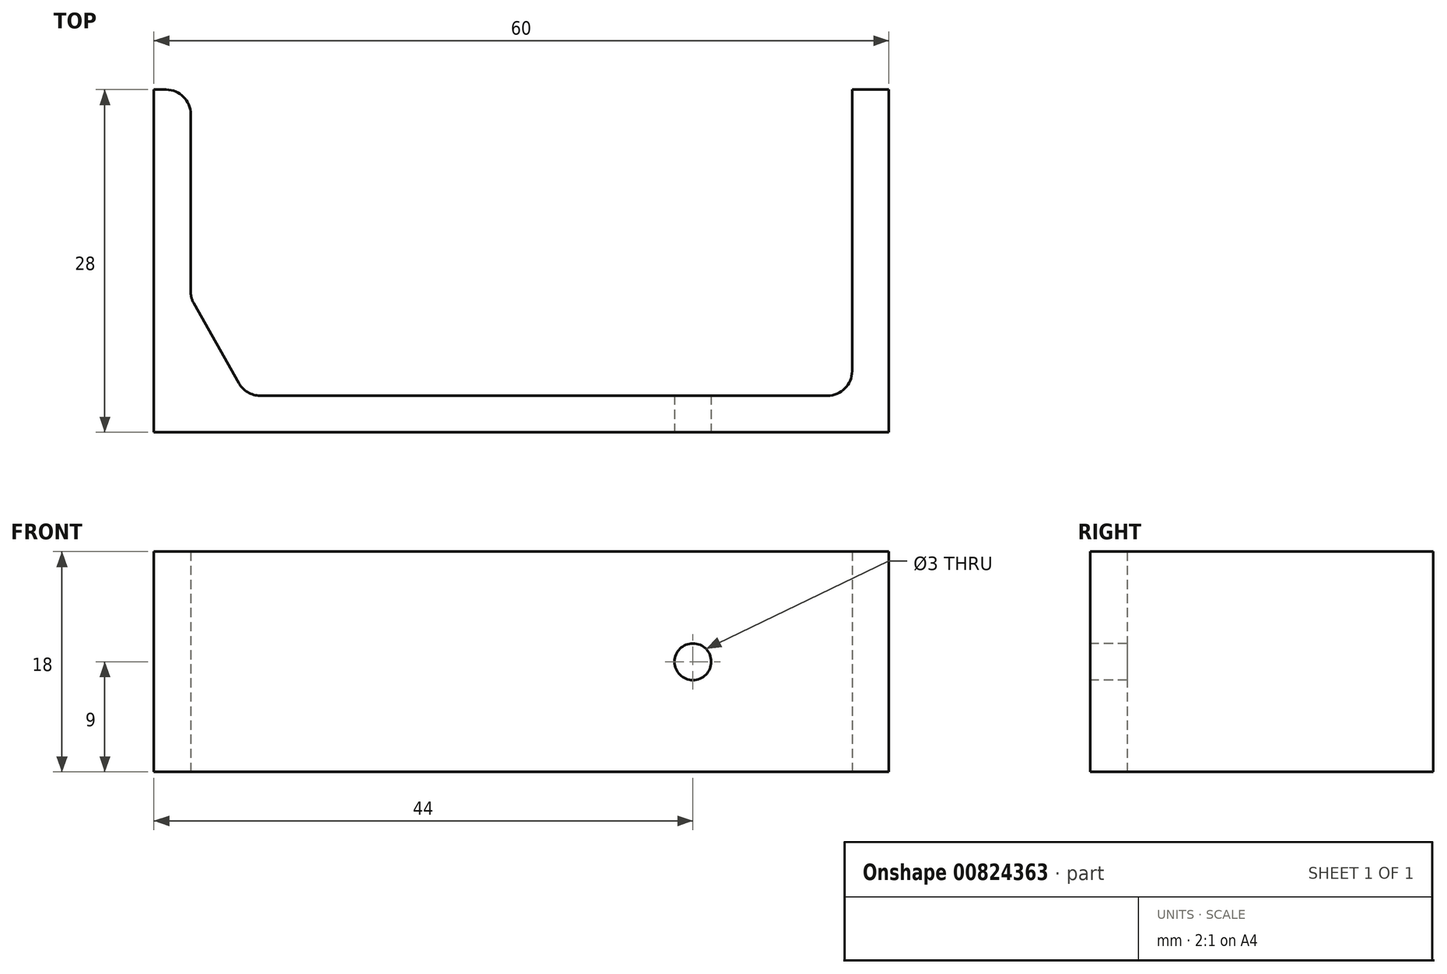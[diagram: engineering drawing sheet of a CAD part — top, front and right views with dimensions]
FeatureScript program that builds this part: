
annotation { "Feature Type Name" : "Feature", "Feature Type Description" : "" }
export const myFeature = defineFeature(function(context is Context, id is Id, definition is map)
    precondition{}
    {
        {
            var Q0;
            Q0=qCreatedBy(makeId("Top.planeOp"),FACE);
            var sketch = newSketch(context, id + "F0", { "sketchPlane" : qUnion([Q0])});
            skLineSegment(sketch, "E0", {"start": v(0, 0) * mm, "end": v(3, 0) * mm});
            skLineSegment(sketch, "E1", {"start": v(3, 0) * mm, "end": v(3, -25) * mm});
            skLineSegment(sketch, "E2", {"start": v(3, -25) * mm, "end": v(57, -25) * mm});
            skLineSegment(sketch, "E3", {"start": v(57, -25) * mm, "end": v(57, 0) * mm});
            skLineSegment(sketch, "E4", {"start": v(57, 0) * mm, "end": v(60, 0) * mm});
            skLineSegment(sketch, "E5", {"start": v(60, 0) * mm, "end": v(60, -28) * mm});
            skLineSegment(sketch, "E6", {"start": v(60, -28) * mm, "end": v(0, -28) * mm});
            skLineSegment(sketch, "E7", {"start": v(0, -28) * mm, "end": v(0, 0) * mm});
            skSolve(sketch);
        }
        {
            var Q0;
            Q0=makeQuery(id+"F0.imprint","IMPRINT",FACE,{"disambiguationData":[TD([[makeQuery(id+"F0.imprint","IMPRINT",EDGE,{"derivedFrom":sQuery(id+"F0.wireOp",EDGE,"E0")}),-1.0]])]});
            extrude(context, id + "F1", {"entities" : qUnion([Q0]), "depth" : 18 * mm, "offsetDistance" : 25 * mm});
        }
        {
            var Q0;
            Q0=makeQuery(id+"F1.opExtrude","SWEPT_FACE",FACE,{"disambiguationData":[OSD([sQuery(id+"F0.wireOp",EDGE,"E6")])]});
            var sketch = newSketch(context, id + "F2", { "sketchPlane" : qUnion([Q0])});
            skLineSegment(sketch, "E8.0.0", {"start": v(0, 0) * mm, "end": v(60, 0) * mm, "construction": true});
            skLineSegment(sketch, "E8.0.1", {"start": v(60, 0) * mm, "end": v(60, 18) * mm, "construction": true});
            skLineSegment(sketch, "E8.0.2", {"start": v(60, 18) * mm, "end": v(0, 18) * mm, "construction": true});
            skLineSegment(sketch, "E8.0.3", {"start": v(0, 18) * mm, "end": v(0, 0) * mm, "construction": true});
            skLineSegment(sketch, "E9", {"start": v(0, 9) * mm, "end": v(60, 9) * mm, "construction": true});
            skCircle(sketch, "E10", {"center": v(44, 9) * mm, "radius": 1.5 * mm});
            skCircle(sketch, "E11", {"center": v(31, 9) * mm, "radius": 1.5 * mm});
            skSolve(sketch);
        }
        {
            var Q0;
            Q0=makeQuery(id+"F2.imprint","IMPRINT",FACE,{"disambiguationData":[TD([[makeQuery(id+"F2.imprint","IMPRINT",EDGE,{"derivedFrom":sQuery(id+"F2.wireOp",EDGE,"E10")}),1.0]])]});
            extrude(context, id + "F3", {"entities" : qUnion([Q0]), "operationType" : NewBodyOperationType.REMOVE, "endBound" : BoundingType.THROUGH_ALL, "oppositeDirection" : true, "depth" : 25 * mm, "offsetDistance" : 25 * mm});
        }
        {
            var Q0;
            Q0=makeQuery(id+"F1.opExtrude","SWEPT_EDGE",EDGE,{"disambiguationData":[OSD([sQuery(id+"F0.wireOp",EDGE,"E1"),sQuery(id+"F0.wireOp",EDGE,"E2")])]});
            chamfer(context, id + "F4", {"entities" : qUnion([Q0]), "chamferType" : ChamferType.TWO_OFFSETS, "width1" : 8 * mm, "oppositeDirection" : false, "width2" : 4.5 * mm, "tangentPropagation" : true});
        }
        {
            var Q0;
            Q0=makeQuery(id+"F1.opExtrude","SWEPT_EDGE",EDGE,{"disambiguationData":[OSD([sQuery(id+"F0.wireOp",EDGE,"E2"),sQuery(id+"F0.wireOp",EDGE,"E3")])]});
            var Q1;
            {var subQ0=sQuery(id+"F0.wireOp",EDGE,"E2");Q1=makeQuery(id+"F4.opChamfer","BLEND_EDGE",EDGE,{"blendedFrom":[makeQuery(id+"F1.opExtrude","SWEPT_EDGE",EDGE,{"disambiguationData":[OSD([sQuery(id+"F0.wireOp",EDGE,"E1"),subQ0])]}),makeQuery(id+"F1.opExtrude","SWEPT_FACE",FACE,{"disambiguationData":[OSD([subQ0])]})],"blendedInto":[makeQuery(id+"F1.opExtrude","SWEPT_FACE",FACE,{"disambiguationData":[OSD([subQ0])]})]});}
            var Q2;
            {var subQ0=sQuery(id+"F0.wireOp",EDGE,"E1");Q2=makeQuery(id+"F4.opChamfer","BLEND_EDGE",EDGE,{"blendedFrom":[makeQuery(id+"F1.opExtrude","SWEPT_EDGE",EDGE,{"disambiguationData":[OSD([subQ0,sQuery(id+"F0.wireOp",EDGE,"E2")])]}),makeQuery(id+"F1.opExtrude","SWEPT_FACE",FACE,{"disambiguationData":[OSD([subQ0])]})],"blendedInto":[makeQuery(id+"F1.opExtrude","SWEPT_FACE",FACE,{"disambiguationData":[OSD([subQ0])]})]});}
            var Q3;
            Q3=makeQuery(id+"F1.opExtrude","SWEPT_EDGE",EDGE,{"disambiguationData":[OSD([sQuery(id+"F0.wireOp",EDGE,"E0"),sQuery(id+"F0.wireOp",EDGE,"E1")])]});
            fillet(context, id + "F5", {"entities" : qUnion([Q0, Q1, Q2, Q3]), "radius" : 2 * mm, "tangentPropagation" : true, "allowEdgeOverflow" : false});
        }
    });
